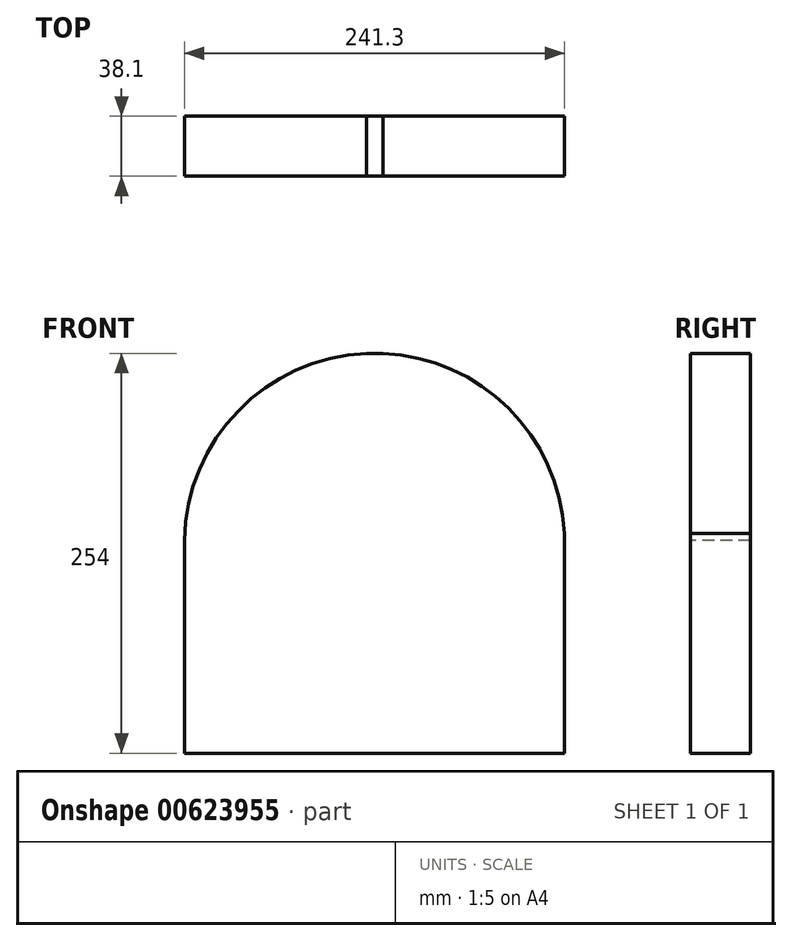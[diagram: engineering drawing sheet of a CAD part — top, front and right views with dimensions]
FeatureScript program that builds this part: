
annotation { "Feature Type Name" : "Feature", "Feature Type Description" : "" }
export const myFeature = defineFeature(function(context is Context, id is Id, definition is map)
    precondition{}
    {
        {
            var Q0;
            Q0=qCreatedBy(makeId("Top.planeOp"),FACE);
            var sketch = newSketch(context, id + "F0", { "sketchPlane" : qUnion([Q0])});
            skLineSegment(sketch, "E0.bottom", {"start": v(-110.6, -148.13) * mm, "end": v(130.7, -148.13) * mm});
            skLineSegment(sketch, "E0.top", {"start": v(-110.6, -110.03) * mm, "end": v(130.7, -110.03) * mm});
            skLineSegment(sketch, "E0.left", {"start": v(-110.6, -148.13) * mm, "end": v(-110.6, -110.03) * mm});
            skLineSegment(sketch, "E0.right", {"start": v(130.7, -148.13) * mm, "end": v(130.7, -110.03) * mm});
            skSolve(sketch);
        }
        {
            var Q0;
            Q0=makeQuery(id+"F0.imprint","IMPRINT",FACE,{"disambiguationData":[TD([[makeQuery(id+"F0.imprint","IMPRINT",EDGE,{"derivedFrom":sQuery(id+"F0.wireOp",EDGE,"E0.bottom")}),1.0]])]});
            extrude(context, id + "F1", {"entities" : qUnion([Q0]), "depth" : 254 * mm, "offsetDistance" : 25.4 * mm});
        }
        {
            var Q0;
            Q0=makeQuery(id+"F1.opExtrude","SWEPT_FACE",FACE,{"disambiguationData":[OSD([sQuery(id+"F0.wireOp",EDGE,"E0.bottom")])]});
            var sketch = newSketch(context, id + "F2", { "sketchPlane" : qUnion([Q0])});
            skArc(sketch, "E1", {"start": v(130.7, 127) * mm, "mid": v(12.44, 254.09) * mm, "end": v(-110.6, 131.6) * mm});
            skSolve(sketch);
        }
        {
            var Q0;
            {var subQ0=sQuery(id+"F2.wireOp",EDGE,"E1");var subQ1=sQuery(id+"F0.wireOp",EDGE,"E0.bottom");var subQ4=makeQuery(id+"F1.opExtrude","CAP_EDGE",EDGE,{"disambiguationData":[OSD([subQ1])],"isStart":false});var subQ5=makeQuery(id+"F2.imprint","INTERSECT",VERTEX,{"disambiguationData":[OD(0.0)],"derivedFrom":[subQ4,subQ0]});Q0=makeQuery(id+"F2.imprint","IMPRINT",FACE,{"disambiguationData":[TD([[makeQuery(id+"F2.imprint","IMPRINT",EDGE,{"disambiguationData":[TD([[subQ5,1.0]])],"derivedFrom":subQ0}),-1.0]])]});}
            var Q1;
            {var subQ0=sQuery(id+"F2.wireOp",EDGE,"E1");var subQ1=sQuery(id+"F0.wireOp",EDGE,"E0.bottom");var subQ2=makeQuery(id+"F1.opExtrude","CAP_EDGE",EDGE,{"disambiguationData":[OSD([subQ1])],"isStart":false});var subQ3=makeQuery(id+"F2.imprint","INTERSECT",VERTEX,{"disambiguationData":[OD(1.0)],"derivedFrom":[subQ2,subQ0]});Q1=makeQuery(id+"F2.imprint","IMPRINT",FACE,{"disambiguationData":[TD([[makeQuery(id+"F2.imprint","IMPRINT",EDGE,{"disambiguationData":[TD([[subQ3,-1.0]])],"derivedFrom":subQ0}),-1.0]])]});}
            extrude(context, id + "F3", {"entities" : qUnion([Q0, Q1]), "operationType" : NewBodyOperationType.REMOVE, "oppositeDirection" : true, "depth" : 38.1 * mm, "offsetDistance" : 25.4 * mm});
        }
    });
